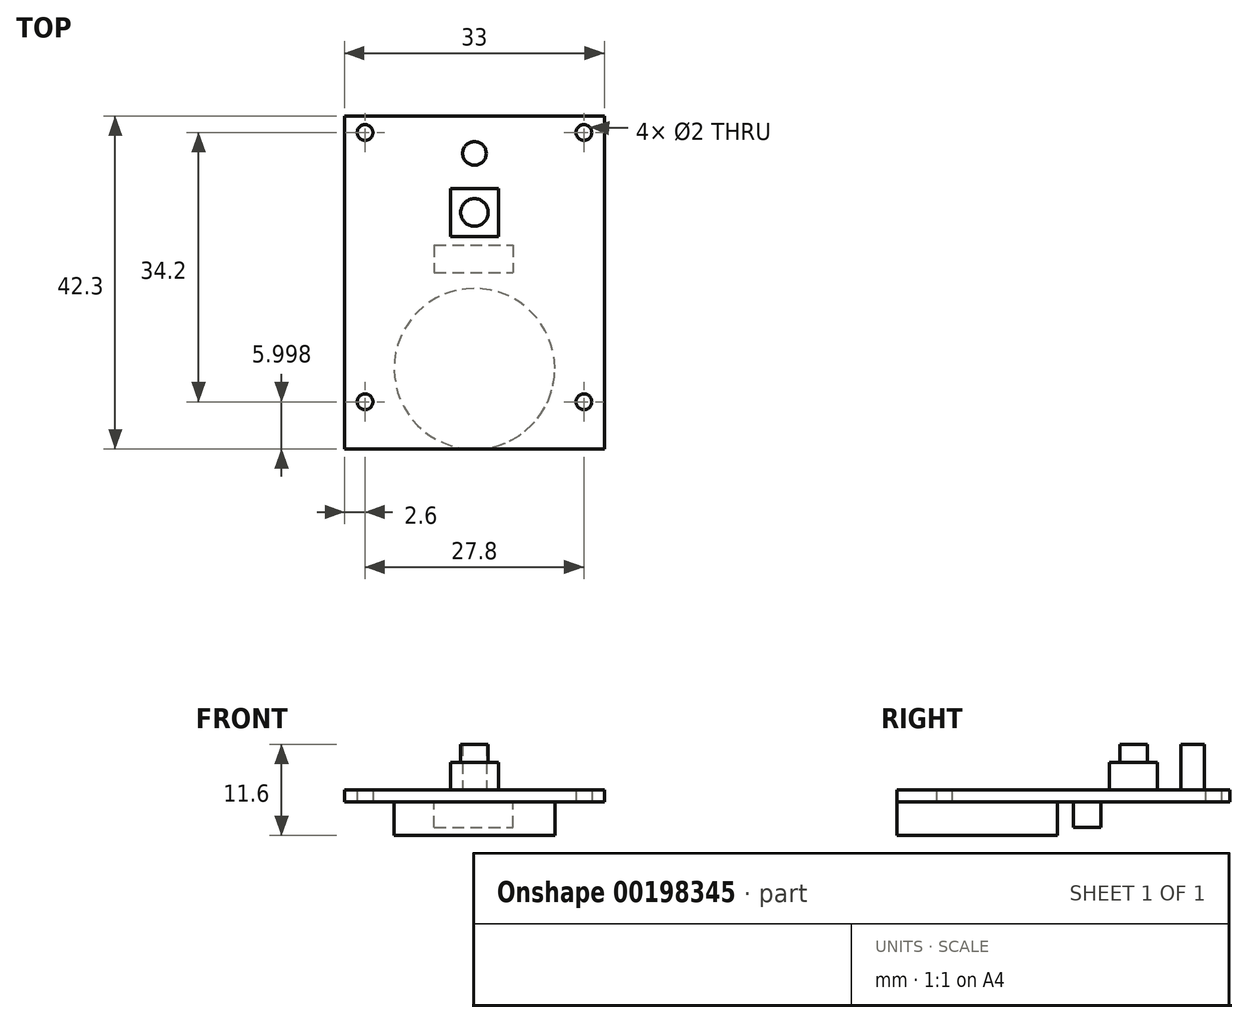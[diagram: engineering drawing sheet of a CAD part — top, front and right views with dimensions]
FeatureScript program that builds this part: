
annotation { "Feature Type Name" : "Feature", "Feature Type Description" : "" }
export const myFeature = defineFeature(function(context is Context, id is Id, definition is map)
    precondition{}
    {
        {
            var Q0;
            Q0=qCreatedBy(makeId("Top.planeOp"),FACE);
            var sketch = newSketch(context, id + "F0", { "sketchPlane" : qUnion([Q0])});
            skLineSegment(sketch, "E0.bottom", {"start": v(-16.5, 24.62) * mm, "end": v(16.5, 24.62) * mm});
            skLineSegment(sketch, "E0.top", {"start": v(-16.5, -17.68) * mm, "end": v(16.5, -17.68) * mm});
            skLineSegment(sketch, "E0.left", {"start": v(-16.5, 24.62) * mm, "end": v(-16.5, -17.68) * mm});
            skLineSegment(sketch, "E0.right", {"start": v(16.5, 24.62) * mm, "end": v(16.5, -17.68) * mm});
            skCircle(sketch, "E1", {"center": v(0, -7.48) * mm, "radius": 10.2 * mm});
            skLineSegment(sketch, "E2", {"start": v(-16.5, -7.48) * mm, "end": v(16.5, -7.48) * mm, "construction": true});
            skCircle(sketch, "E3", {"center": v(0, 19.87) * mm, "radius": 1.5 * mm});
            skCircle(sketch, "E4", {"center": v(0, 12.37) * mm, "radius": 1.75 * mm});
            skLineSegment(sketch, "E5.bottom", {"start": v(-3.05, 15.42) * mm, "end": v(3.05, 15.42) * mm});
            skLineSegment(sketch, "E5.top", {"start": v(-3.05, 9.32) * mm, "end": v(3.05, 9.32) * mm});
            skLineSegment(sketch, "E5.left", {"start": v(-3.05, 15.42) * mm, "end": v(-3.05, 9.32) * mm});
            skLineSegment(sketch, "E5.right", {"start": v(3.05, 15.42) * mm, "end": v(3.05, 9.32) * mm});
            skLineSegment(sketch, "E6", {"start": v(-3.05, 15.42) * mm, "end": v(3.05, 9.32) * mm, "construction": true});
            skLineSegment(sketch, "E7.bottom", {"start": v(-5.11, 8.22) * mm, "end": v(4.89, 8.22) * mm});
            skLineSegment(sketch, "E7.top", {"start": v(-5.11, 4.72) * mm, "end": v(4.89, 4.72) * mm});
            skLineSegment(sketch, "E7.left", {"start": v(-5.11, 8.22) * mm, "end": v(-5.11, 4.72) * mm});
            skLineSegment(sketch, "E7.right", {"start": v(4.89, 8.22) * mm, "end": v(4.89, 4.72) * mm});
            skCircle(sketch, "E8", {"center": v(13.9, 22.52) * mm, "radius": 1 * mm});
            skCircle(sketch, "E9", {"center": v(-13.9, 22.52) * mm, "radius": 1 * mm});
            skCircle(sketch, "E10", {"center": v(13.9, -11.68) * mm, "radius": 1 * mm});
            skCircle(sketch, "E11", {"center": v(-13.9, -11.68) * mm, "radius": 1 * mm});
            skSolve(sketch);
        }
        {
            var Q0;
            Q0=makeQuery(id+"F0.imprint","IMPRINT",FACE,{"disambiguationData":[TD([[makeQuery(id+"F0.imprint","IMPRINT",EDGE,{"derivedFrom":sQuery(id+"F0.wireOp",EDGE,"E0.bottom")}),-1.0]])]});
            var Q1;
            Q1=makeQuery(id+"F0.imprint","IMPRINT",FACE,{"disambiguationData":[TD([[makeQuery(id+"F0.imprint","IMPRINT",EDGE,{"derivedFrom":sQuery(id+"F0.wireOp",EDGE,"E1")}),1.0]])]});
            var Q2;
            Q2=makeQuery(id+"F0.imprint","IMPRINT",FACE,{"disambiguationData":[TD([[makeQuery(id+"F0.imprint","IMPRINT",EDGE,{"derivedFrom":sQuery(id+"F0.wireOp",EDGE,"E3")}),1.0]])]});
            var Q3;
            Q3=makeQuery(id+"F0.imprint","IMPRINT",FACE,{"disambiguationData":[TD([[makeQuery(id+"F0.imprint","IMPRINT",EDGE,{"derivedFrom":sQuery(id+"F0.wireOp",EDGE,"E4")}),-1.0]])]});
            var Q4;
            Q4=makeQuery(id+"F0.imprint","IMPRINT",FACE,{"disambiguationData":[TD([[makeQuery(id+"F0.imprint","IMPRINT",EDGE,{"derivedFrom":sQuery(id+"F0.wireOp",EDGE,"E4")}),1.0]])]});
            var Q5;
            Q5=makeQuery(id+"F0.imprint","IMPRINT",FACE,{"disambiguationData":[TD([[makeQuery(id+"F0.imprint","IMPRINT",EDGE,{"derivedFrom":sQuery(id+"F0.wireOp",EDGE,"E7.bottom")}),-1.0]])]});
            extrude(context, id + "F1", {"entities" : qUnion([Q0, Q1, Q2, Q3, Q4, Q5]), "depth" : 1.5 * mm});
        }
        {
            var Q0;
            Q0=makeQuery(id+"F0.imprint","IMPRINT",FACE,{"disambiguationData":[TD([[makeQuery(id+"F0.imprint","IMPRINT",EDGE,{"derivedFrom":sQuery(id+"F0.wireOp",EDGE,"E1")}),1.0]])]});
            extrude(context, id + "F2", {"entities" : qUnion([Q0]), "operationType" : NewBodyOperationType.ADD, "oppositeDirection" : true, "depth" : 4.3 * mm});
        }
        {
            var Q0;
            Q0=makeQuery(id+"F0.imprint","IMPRINT",FACE,{"disambiguationData":[TD([[makeQuery(id+"F0.imprint","IMPRINT",EDGE,{"derivedFrom":sQuery(id+"F0.wireOp",EDGE,"E3")}),1.0]])]});
            var Q1;
            Q1=makeQuery(id+"F0.imprint","IMPRINT",FACE,{"disambiguationData":[TD([[makeQuery(id+"F0.imprint","IMPRINT",EDGE,{"derivedFrom":sQuery(id+"F0.wireOp",EDGE,"E4")}),1.0]])]});
            extrude(context, id + "F3", {"entities" : qUnion([Q0, Q1]), "operationType" : NewBodyOperationType.ADD, "depth" : 7.3 * mm});
        }
        {
            var Q0;
            Q0=makeQuery(id+"F0.imprint","IMPRINT",FACE,{"disambiguationData":[TD([[makeQuery(id+"F0.imprint","IMPRINT",EDGE,{"derivedFrom":sQuery(id+"F0.wireOp",EDGE,"E4")}),-1.0]])]});
            extrude(context, id + "F4", {"entities" : qUnion([Q0]), "operationType" : NewBodyOperationType.ADD, "depth" : 5 * mm});
        }
        {
            var Q0;
            Q0=makeQuery(id+"F0.imprint","IMPRINT",FACE,{"disambiguationData":[TD([[makeQuery(id+"F0.imprint","IMPRINT",EDGE,{"derivedFrom":sQuery(id+"F0.wireOp",EDGE,"E7.bottom")}),-1.0]])]});
            extrude(context, id + "F5", {"entities" : qUnion([Q0]), "operationType" : NewBodyOperationType.ADD, "oppositeDirection" : true, "depth" : 3.3 * mm});
        }
    });
